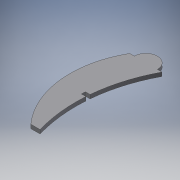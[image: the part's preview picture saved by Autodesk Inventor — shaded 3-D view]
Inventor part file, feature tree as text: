
AUTODESK INVENTOR PART (.ipt)
format: ipt  version: 2017 (Build 210142000, 142)  size: 113,664 bytes
history: native  units: mm
features: extrude x2, sketch x2
ambient origin geometry x8: Origin, YZ Plane, XZ Plane, XY Plane, X Axis, Y Axis, Z Axis, Center Point
bodies: Solid1 (feature_tree)
feature tree (4):
  extrude  "Extrusion1"  Depth=12.7mm
  extrude  "Extrusion2"  Depth=5.3mm TaperAngle=0.0deg
  sketch  "Sketch1"  dims[d0=31.75mm d1=12.7mm]
  sketch  "Sketch2"  dims[d2=152.4mm d3=5.3mm d4=0.0mm d5=5.3mm d6=88.9mm d7=3.81mm d8=0.0mm d9=70.0mm]
